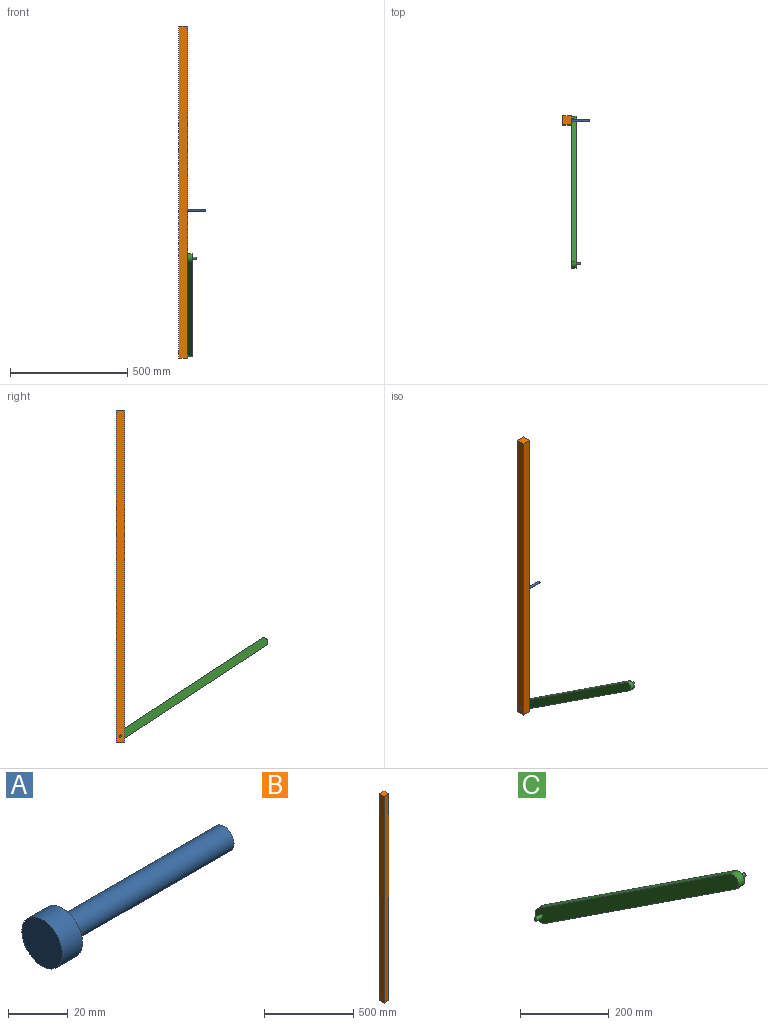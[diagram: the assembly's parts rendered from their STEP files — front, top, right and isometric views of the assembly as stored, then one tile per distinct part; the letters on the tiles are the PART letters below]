
ASSEMBLY  parts=3 mates=2
PART A: 5 faces, bbox 85.7x19.1x19.1 mm
  f0: cylinder r=9.53mm len=19.05mm, axis (1,0,0), area 570mm2, adj f1,f2
  f1: plane 19.05x19.05mm, normal (-1,0,0), area 285mm2, adj f0
  f2: plane 19.05x19.05mm, normal (1,0,0), area 213.8mm2, adj f0,f3
  f3: cylinder r=4.76mm len=76.2mm, axis (-1,0,0), area 2280.2mm2, adj f2,f4
  f4: plane 9.53x9.53mm, normal (1,0,0), area 71.3mm2, adj f3
PART B: 12 faces, bbox 38.1x38.1x1414.9 mm
  f0: plane 1414.95x38.1mm, normal (0,1,0), area 53909.4mm2, adj f1,f3,f5,f6
  f1: plane 38.1x38.1mm, normal (0,0,-1), area 1451.6mm2, adj f0,f2,f5,f6
  f2: plane 1414.95x38.1mm, normal (0,-1,0), area 53909.4mm2, adj f1,f3,f5,f6
  f3: plane 38.1x38.1mm, normal (0,0,1), area 1451.6mm2, adj f0,f2,f5,f6
  f4: cylinder r=4.76mm len=38.1mm, axis (1,0,0), area 1140.1mm2, adj f5,f6
  f5: plane 1414.95x38.1mm, normal (-1,0,0), area 53838.1mm2, adj f0,f1,f2,f3,f4
  f6: plane 1414.95x38.1mm, normal (1,0,0), area 35671mm2, adj f0,f1,f2,f3,f4,f7,f8,f9
  f7: cylinder r=9.53mm len=19.05mm, axis (1,0,0), area 380mm2, adj f6,f8,f10,f11
  f8: plane 938.7x12.7mm, normal (0,-1,0), area 11921.4mm2, adj f6,f7,f9,f11
  f9: cylinder r=9.53mm len=19.05mm, axis (1,0,0), area 380mm2, adj f6,f8,f10,f11
  f10: plane 938.7x12.7mm, normal (0,1,0), area 11921.4mm2, adj f6,f7,f9,f11
  f11: plane 957.75x19.05mm, normal (1,0,0), area 18167.2mm2, adj f7,f8,f9,f10
PART C: 10 faces, bbox 57.2x647.7x438.2 mm
  f0: plane 609.6x400.05mm, normal (0,0.55,0.84), area 13890.2mm2, adj f1,f3,f4,f5
  f1: cylinder r=19.05mm len=34.98mm, axis (-1,0,0), area 1140.1mm2, adj f0,f2,f4,f5
  f2: plane 609.6x400.05mm, normal (0,-0.55,-0.84), area 13890.2mm2, adj f1,f3,f4,f5
  f3: cylinder r=19.05mm len=34.98mm, axis (-1,0,0), area 1140.1mm2, adj f0,f2,f4,f5
  f4: plane 647.7x438.15mm, normal (1,0,0), area 28849.3mm2, adj f0,f1,f2,f3,f6
  f5: plane 647.7x438.15mm, normal (-1,0,0), area 28849.3mm2, adj f0,f1,f2,f3,f9
  f6: cylinder r=4.76mm len=19.05mm, axis (-1,0,0), area 570mm2, adj f4,f7
  f7: plane 9.53x9.53mm, normal (1,0,0), area 71.3mm2, adj f6
  f8: plane 9.53x9.53mm, normal (-1,0,0), area 71.3mm2, adj f9
  f9: cylinder r=4.76mm len=19.05mm, axis (-1,0,0), area 570mm2, adj f5,f8
PLACE A t=(217.46,-727.07,36.43)mm
PLACE B t=(217.46,-727.07,-166.47)mm
PLACE C t=(217.46,-727.07,-166.47)mm
MATE planar A.f0 <-> B.f9  axis (1,0,0) through (-592.17,-279.4,17.38)mm
MATE revolute C.f1 <-> B.f4  axis (-1,0,0) through (-592.17,-279.4,-585.57)mm
